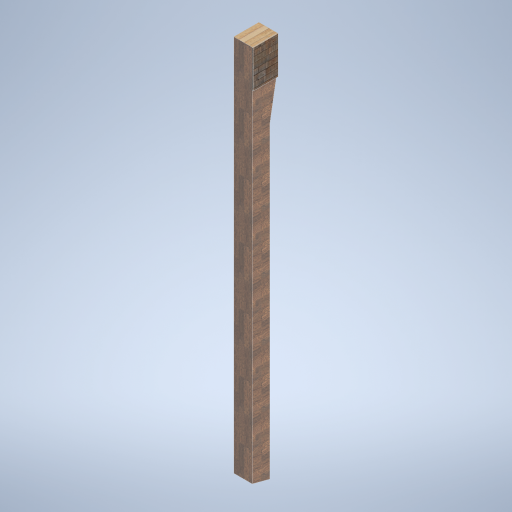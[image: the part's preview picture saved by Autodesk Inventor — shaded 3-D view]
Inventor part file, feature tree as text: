
AUTODESK INVENTOR PART (.ipt)
format: ipt  version: 2024.2 (Build 282272000, 272)  size: 313,856 bytes
history: native  units: in
note: dims shown in document units (in); Inventor stores cm internally (conversion verified against a paired STEP export)
features: other x3, sketch x1
ambient origin geometry x8: Origin, YZ Plane, XZ Plane, XY Plane, X Axis, Y Axis, Z Axis, Center Point
bodies: Solid1 (feature_tree)
feature tree (4):
  other  "side_pillar_02_MIR.ipt"
  other  "Solid1::side_pillar_02_MIR.ipt"
  other  "TaggingFeature1"
  sketch  "Sketch3"  dims[d0=0.3937in]
